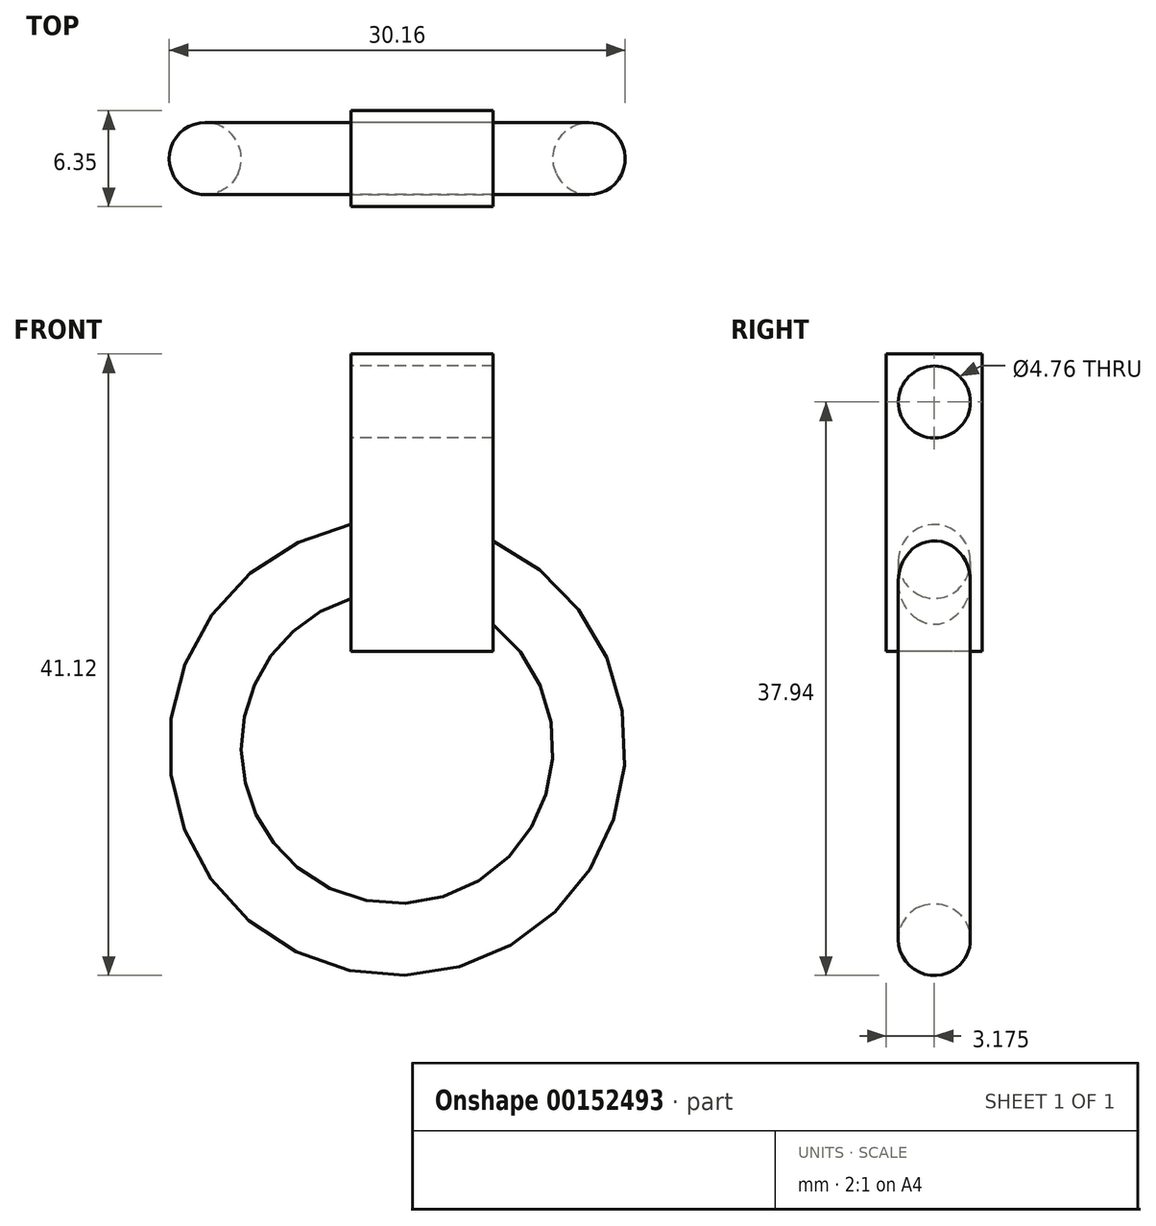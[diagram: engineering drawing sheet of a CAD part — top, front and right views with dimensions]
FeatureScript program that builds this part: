
annotation { "Feature Type Name" : "Feature", "Feature Type Description" : "" }
export const myFeature = defineFeature(function(context is Context, id is Id, definition is map)
    precondition{}
    {
        {
            var Q0;
            Q0=qCreatedBy(makeId("Right.planeOp"),FACE);
            var sketch = newSketch(context, id + "F0", { "sketchPlane" : qUnion([Q0])});
            skLineSegment(sketch, "E0.bottom", {"start": v(0, 0) * mm, "end": v(-6.35, 0) * mm});
            skLineSegment(sketch, "E0.top", {"start": v(0, 19.68) * mm, "end": v(-6.35, 19.68) * mm});
            skLineSegment(sketch, "E0.left", {"start": v(0, 0) * mm, "end": v(0, 19.68) * mm});
            skLineSegment(sketch, "E0.right", {"start": v(-6.35, 0) * mm, "end": v(-6.35, 19.68) * mm});
            skCircle(sketch, "E1", {"center": v(-3.18, 16.51) * mm, "radius": 2.38 * mm});
            skSolve(sketch);
        }
        {
            var Q0;
            Q0 = qSketchRegion(id + "F0", true);
            extrude(context, id + "F1", {"entities" : qUnion([Q0]), "depth" : 3.05 * mm});
        }
        {
            var Q0;
            Q0=makeQuery(id+"F1.opExtrude","CAP_FACE",FACE,{"disambiguationData":[OSD([sQuery(id+"F0.wireOp",EDGE,"E0.bottom"),sQuery(id+"F0.wireOp",EDGE,"E0.top"),sQuery(id+"F0.wireOp",EDGE,"E0.left"),sQuery(id+"F0.wireOp",EDGE,"E0.right"),sQuery(id+"F0.wireOp",EDGE,"E1"),sQuery(id+"F0.wireOp",EDGE,"mSoTqHci-z2N1-n1Bf-S6DM-xwMpXsOgpsCP")])],"isStart":false});
            var sketch = newSketch(context, id + "F2", { "sketchPlane" : qUnion([Q0])});
            skLineSegment(sketch, "E2", {"start": v(-3.17, 6.35) * mm, "end": v(-3.17, -6.35) * mm});
            skCircle(sketch, "E3", {"center": v(-3.17, 6.35) * mm, "radius": 2.38 * mm});
            skLineSegment(sketch, "E4", {"start": v(-3.17, -6.35) * mm, "end": v(-7.37, -6.35) * mm});
            skSolve(sketch);
        }
        {
            var Q0;
            Q0=makeQuery(id+"F2.imprint","IMPRINT",FACE,{"disambiguationData":[TD([[makeQuery(id+"F2.imprint","IMPRINT",EDGE,{"derivedFrom":sQuery(id+"F2.wireOp",EDGE,"E3")}),1.0]])]});
            var Q1;
            Q1=sQuery(id+"F2.wireOp",EDGE,"E4");
            revolve(context, id + "F3", {"operationType" : NewBodyOperationType.ADD, "entities" : qUnion([Q0]), "axis" : qUnion([Q1]), "revolveType" : RevolveType.TWO_DIRECTIONS, "angle" : 359 * degree, "angleBack" : 10 * degree});
        }
        {
            var Q0;
            Q0=makeQuery(id+"F1.opExtrude","CAP_FACE",FACE,{"disambiguationData":[OSD([sQuery(id+"F0.wireOp",EDGE,"E0.bottom"),sQuery(id+"F0.wireOp",EDGE,"E0.top"),sQuery(id+"F0.wireOp",EDGE,"E0.left"),sQuery(id+"F0.wireOp",EDGE,"E0.right"),sQuery(id+"F0.wireOp",EDGE,"E1")])],"isStart":false});
            var sketch = newSketch(context, id + "F4", { "sketchPlane" : qUnion([Q0])});
            skLineSegment(sketch, "E5.bottom", {"start": v(-6.35, 19.68) * mm, "end": v(0, 19.68) * mm});
            skLineSegment(sketch, "E5.top", {"start": v(-6.35, 0) * mm, "end": v(0, 0) * mm});
            skLineSegment(sketch, "E5.left", {"start": v(-6.35, 19.68) * mm, "end": v(-6.35, 0) * mm});
            skLineSegment(sketch, "E5.right", {"start": v(0, 19.68) * mm, "end": v(0, 0) * mm});
            skCircle(sketch, "E6", {"center": v(-3.18, 16.51) * mm, "radius": 2.38 * mm});
            skSolve(sketch);
        }
        {
            var Q0;
            Q0 = qSketchRegion(id + "F4", true);
            extrude(context, id + "F5", {"entities" : qUnion([Q0]), "operationType" : NewBodyOperationType.ADD, "depth" : 6.35 * mm});
        }
    });
